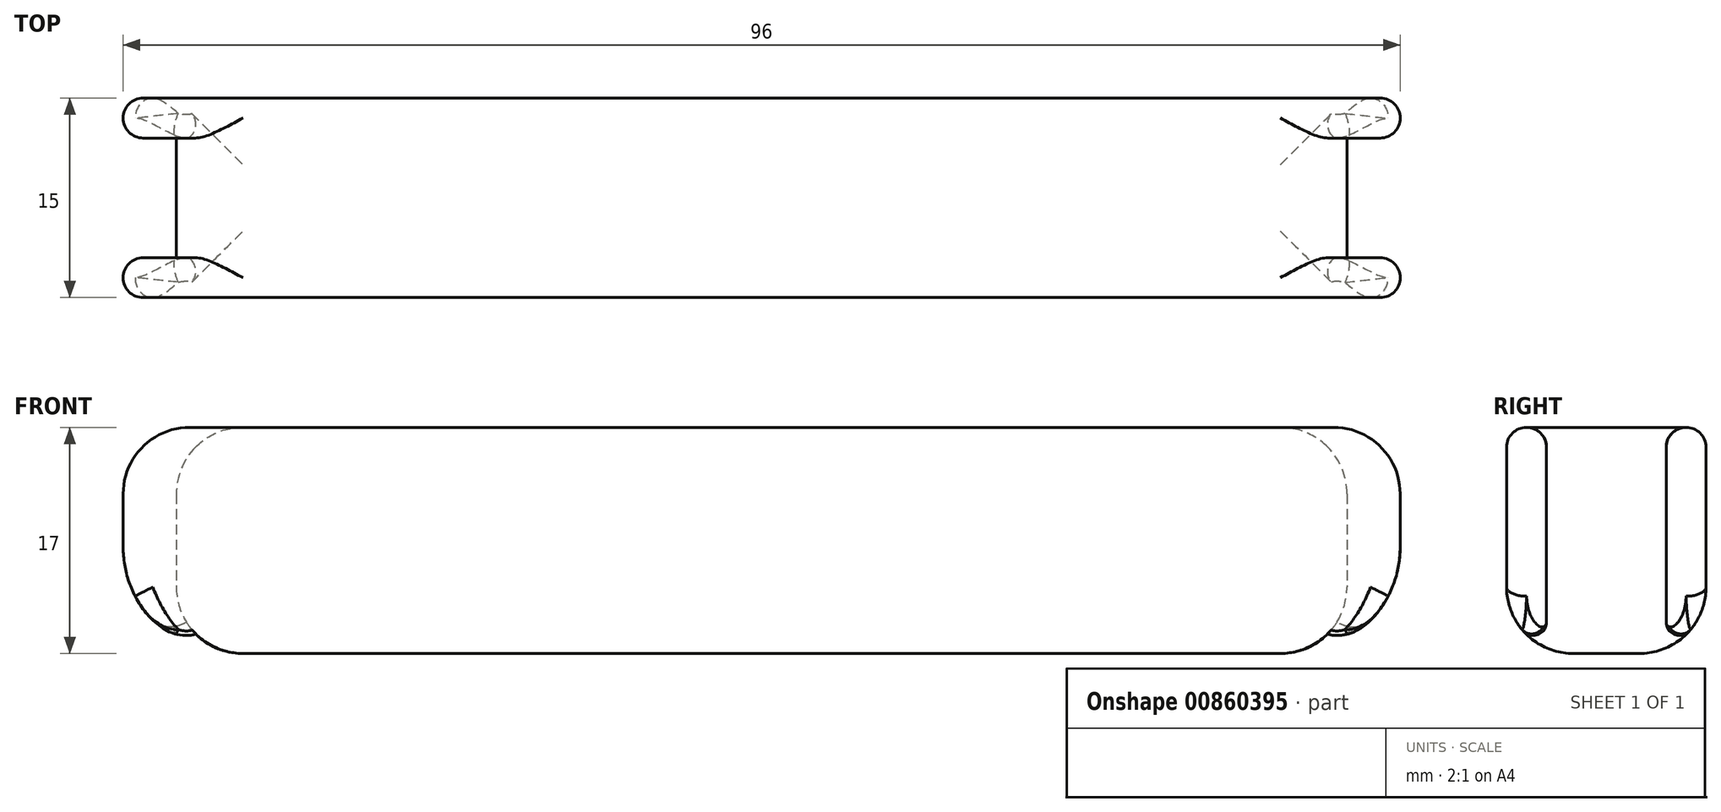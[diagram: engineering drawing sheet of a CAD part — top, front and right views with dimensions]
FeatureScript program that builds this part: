
annotation { "Feature Type Name" : "Feature", "Feature Type Description" : "" }
export const myFeature = defineFeature(function(context is Context, id is Id, definition is map)
    precondition{}
    {
        {
            var Q0;
            Q0=qCreatedBy(makeId("Top.planeOp"),FACE);
            var sketch = newSketch(context, id + "F0", { "sketchPlane" : qUnion([Q0])});
            skLineSegment(sketch, "E0.bottom", {"start": v(48, -7.5) * mm, "end": v(-48, -7.5) * mm});
            skLineSegment(sketch, "E0.top", {"start": v(48, 7.5) * mm, "end": v(-48, 7.5) * mm});
            skLineSegment(sketch, "E0.left", {"start": v(48, -7.5) * mm, "end": v(48, 7.5) * mm});
            skLineSegment(sketch, "E0.right", {"start": v(-48, -7.5) * mm, "end": v(-48, 7.5) * mm});
            skPoint(sketch, "E0.middle", {"position": v(0, 0) * mm});
            skLineSegment(sketch, "E1.bottom", {"start": v(-48, 4.5) * mm, "end": v(-44, 4.5) * mm});
            skLineSegment(sketch, "E1.top", {"start": v(-48, -4.5) * mm, "end": v(-44, -4.5) * mm});
            skLineSegment(sketch, "E1.left", {"start": v(-48, 4.5) * mm, "end": v(-48, -4.5) * mm});
            skLineSegment(sketch, "E1.right", {"start": v(-44, 4.5) * mm, "end": v(-44, -4.5) * mm});
            skLineSegment(sketch, "E2.bottom", {"start": v(48, 4.5) * mm, "end": v(44, 4.5) * mm});
            skLineSegment(sketch, "E2.top", {"start": v(48, -4.5) * mm, "end": v(44, -4.5) * mm});
            skLineSegment(sketch, "E2.left", {"start": v(48, 4.5) * mm, "end": v(48, -4.5) * mm});
            skLineSegment(sketch, "E2.right", {"start": v(44, 4.5) * mm, "end": v(44, -4.5) * mm});
            skSolve(sketch);
        }
        {
            var Q0;
            {var subQ6=sQuery(id+"F0.wireOp",EDGE,"E0.bottom");Q0=makeQuery(id+"F0.imprint","IMPRINT",FACE,{"disambiguationData":[TD([[makeQuery(id+"F0.imprint","IMPRINT",EDGE,{"derivedFrom":subQ6}),-1.0]])]});}
            extrude(context, id + "F1", {"entities" : qUnion([Q0]), "depth" : 17 * mm, "offsetDistance" : 25 * mm});
        }
        {
            var Q0;
            {var subQ0=sQuery(id+"F0.wireOp",EDGE,"E0.left");Q0=makeQuery(id+"F1.opExtrude","CAP_EDGE",EDGE,{"disambiguationData":[OSD([subQ0]),TDD([makeQuery(id+"F0.imprint","IMPRINT",EDGE,{"disambiguationData":[TD([[makeQuery(id+"F0.imprint","INTERSECT",VERTEX,{"derivedFrom":[sQuery(id+"F0.wireOp",EDGE,"E0.bottom"),subQ0]}),-1.0]])],"derivedFrom":subQ0})])],"isStart":true});}
            var Q1;
            {var subQ0=sQuery(id+"F0.wireOp",EDGE,"E0.left");Q1=makeQuery(id+"F1.opExtrude","CAP_EDGE",EDGE,{"disambiguationData":[OSD([subQ0]),TDD([makeQuery(id+"F0.imprint","IMPRINT",EDGE,{"disambiguationData":[TD([[makeQuery(id+"F0.imprint","INTERSECT",VERTEX,{"derivedFrom":[sQuery(id+"F0.wireOp",EDGE,"E0.top"),subQ0]}),1.0]])],"derivedFrom":subQ0})])],"isStart":true});}
            var Q2;
            {var subQ0=sQuery(id+"F0.wireOp",EDGE,"E0.right");Q2=makeQuery(id+"F1.opExtrude","CAP_EDGE",EDGE,{"disambiguationData":[OSD([subQ0]),TDD([makeQuery(id+"F0.imprint","IMPRINT",EDGE,{"disambiguationData":[TD([[makeQuery(id+"F0.imprint","INTERSECT",VERTEX,{"derivedFrom":[sQuery(id+"F0.wireOp",EDGE,"E0.top"),subQ0]}),1.0]])],"derivedFrom":subQ0})])],"isStart":true});}
            var Q3;
            {var subQ0=sQuery(id+"F0.wireOp",EDGE,"E0.right");Q3=makeQuery(id+"F1.opExtrude","CAP_EDGE",EDGE,{"disambiguationData":[OSD([subQ0]),TDD([makeQuery(id+"F0.imprint","IMPRINT",EDGE,{"disambiguationData":[TD([[makeQuery(id+"F0.imprint","INTERSECT",VERTEX,{"derivedFrom":[sQuery(id+"F0.wireOp",EDGE,"E0.bottom"),subQ0]}),-1.0]])],"derivedFrom":subQ0})])],"isStart":true});}
            fillet(context, id + "F2", {"entities" : qUnion([Q0, Q1, Q2, Q3]), "radius" : 8 * mm, "tangentPropagation" : true, "allowEdgeOverflow" : false});
        }
        {
            var Q0;
            {var subQ0=sQuery(id+"F0.wireOp",EDGE,"E0.right");Q0=makeQuery(id+"F2.opFillet","BLEND_EDGE",EDGE,{"blendedFrom":[makeQuery(id+"F1.opExtrude","CAP_EDGE",EDGE,{"disambiguationData":[OSD([subQ0]),TDD([makeQuery(id+"F0.imprint","IMPRINT",EDGE,{"disambiguationData":[TD([[makeQuery(id+"F0.imprint","INTERSECT",VERTEX,{"derivedFrom":[sQuery(id+"F0.wireOp",EDGE,"E0.top"),subQ0]}),1.0]])],"derivedFrom":subQ0})])],"isStart":true}),makeQuery(id+"F1.opExtrude","SWEPT_FACE",FACE,{"disambiguationData":[OSD([sQuery(id+"F0.wireOp",EDGE,"E1.right")])]})],"blendedInto":[makeQuery(id+"F1.opExtrude","SWEPT_FACE",FACE,{"disambiguationData":[OSD([sQuery(id+"F0.wireOp",EDGE,"E1.right")])]})]});}
            var Q1;
            {var subQ0=sQuery(id+"F0.wireOp",EDGE,"E0.left");Q1=makeQuery(id+"F2.opFillet","BLEND_EDGE",EDGE,{"blendedFrom":[makeQuery(id+"F1.opExtrude","CAP_EDGE",EDGE,{"disambiguationData":[OSD([subQ0]),TDD([makeQuery(id+"F0.imprint","IMPRINT",EDGE,{"disambiguationData":[TD([[makeQuery(id+"F0.imprint","INTERSECT",VERTEX,{"derivedFrom":[sQuery(id+"F0.wireOp",EDGE,"E0.bottom"),subQ0]}),-1.0]])],"derivedFrom":subQ0})])],"isStart":true}),makeQuery(id+"F1.opExtrude","SWEPT_FACE",FACE,{"disambiguationData":[OSD([sQuery(id+"F0.wireOp",EDGE,"E2.right")])]})],"blendedInto":[makeQuery(id+"F1.opExtrude","SWEPT_FACE",FACE,{"disambiguationData":[OSD([sQuery(id+"F0.wireOp",EDGE,"E2.right")])]})]});}
            var Q2;
            Q2=makeQuery(id+"F1.opExtrude","CAP_EDGE",EDGE,{"disambiguationData":[OSD([sQuery(id+"F0.wireOp",EDGE,"E1.right")])],"isStart":false});
            var Q3;
            Q3=makeQuery(id+"F1.opExtrude","CAP_EDGE",EDGE,{"disambiguationData":[OSD([sQuery(id+"F0.wireOp",EDGE,"E2.right")])],"isStart":false});
            fillet(context, id + "F3", {"entities" : qUnion([Q0, Q1, Q2, Q3]), "radius" : 5 * mm, "allowEdgeOverflow" : false});
        }
        {
            var Q0;
            Q0=makeQuery(id+"F1.opExtrude","CAP_EDGE",EDGE,{"disambiguationData":[OSD([sQuery(id+"F0.wireOp",EDGE,"E0.top")])],"isStart":true});
            var Q1;
            Q1=makeQuery(id+"F1.opExtrude","CAP_EDGE",EDGE,{"disambiguationData":[OSD([sQuery(id+"F0.wireOp",EDGE,"E0.bottom")])],"isStart":true});
            var Q2;
            {var subQ0=sQuery(id+"F0.wireOp",EDGE,"E0.right");Q2=makeQuery(id+"F1.opExtrude","CAP_EDGE",EDGE,{"disambiguationData":[OSD([subQ0]),TDD([makeQuery(id+"F0.imprint","IMPRINT",EDGE,{"disambiguationData":[TD([[makeQuery(id+"F0.imprint","INTERSECT",VERTEX,{"derivedFrom":[sQuery(id+"F0.wireOp",EDGE,"E0.top"),subQ0]}),1.0]])],"derivedFrom":subQ0})])],"isStart":false});}
            var Q3;
            {var subQ0=sQuery(id+"F0.wireOp",EDGE,"E0.right");Q3=makeQuery(id+"F1.opExtrude","CAP_EDGE",EDGE,{"disambiguationData":[OSD([subQ0]),TDD([makeQuery(id+"F0.imprint","IMPRINT",EDGE,{"disambiguationData":[TD([[makeQuery(id+"F0.imprint","INTERSECT",VERTEX,{"derivedFrom":[sQuery(id+"F0.wireOp",EDGE,"E0.bottom"),subQ0]}),-1.0]])],"derivedFrom":subQ0})])],"isStart":false});}
            var Q4;
            {var subQ0=sQuery(id+"F0.wireOp",EDGE,"E0.left");Q4=makeQuery(id+"F1.opExtrude","CAP_EDGE",EDGE,{"disambiguationData":[OSD([subQ0]),TDD([makeQuery(id+"F0.imprint","IMPRINT",EDGE,{"disambiguationData":[TD([[makeQuery(id+"F0.imprint","INTERSECT",VERTEX,{"derivedFrom":[sQuery(id+"F0.wireOp",EDGE,"E0.top"),subQ0]}),1.0]])],"derivedFrom":subQ0})])],"isStart":false});}
            var Q5;
            {var subQ0=sQuery(id+"F0.wireOp",EDGE,"E0.left");Q5=makeQuery(id+"F1.opExtrude","CAP_EDGE",EDGE,{"disambiguationData":[OSD([subQ0]),TDD([makeQuery(id+"F0.imprint","IMPRINT",EDGE,{"disambiguationData":[TD([[makeQuery(id+"F0.imprint","INTERSECT",VERTEX,{"derivedFrom":[sQuery(id+"F0.wireOp",EDGE,"E0.bottom"),subQ0]}),-1.0]])],"derivedFrom":subQ0})])],"isStart":false});}
            fillet(context, id + "F4", {"entities" : qUnion([Q0, Q1, Q2, Q3, Q4, Q5]), "radius" : 5 * mm, "allowEdgeOverflow" : false});
        }
        {
            var Q0;
            Q0=makeQuery(id+"F1.opExtrude","SWEPT_EDGE",EDGE,{"disambiguationData":[OSD([sQuery(id+"F0.wireOp",EDGE,"E0.top"),sQuery(id+"F0.wireOp",EDGE,"E0.right")])]});
            var Q1;
            Q1=makeQuery(id+"F1.opExtrude","SWEPT_EDGE",EDGE,{"disambiguationData":[OSD([sQuery(id+"F0.wireOp",EDGE,"E0.right"),sQuery(id+"F0.wireOp",EDGE,"E1.bottom"),sQuery(id+"F0.wireOp",EDGE,"E1.left")])]});
            var Q2;
            Q2=makeQuery(id+"F1.opExtrude","SWEPT_EDGE",EDGE,{"disambiguationData":[OSD([sQuery(id+"F0.wireOp",EDGE,"E0.right"),sQuery(id+"F0.wireOp",EDGE,"E1.top"),sQuery(id+"F0.wireOp",EDGE,"E1.left")])]});
            var Q3;
            {var subQ0=sQuery(id+"F0.wireOp",EDGE,"E0.bottom");var subQ1=sQuery(id+"F0.wireOp",EDGE,"E0.right");Q3=makeQuery(id+"F4.opFillet","BLEND_EDGE",EDGE,{"blendedFrom":[makeQuery(id+"F1.opExtrude","CAP_EDGE",EDGE,{"disambiguationData":[OSD([subQ1]),TDD([makeQuery(id+"F0.imprint","IMPRINT",EDGE,{"disambiguationData":[TD([[makeQuery(id+"F0.imprint","INTERSECT",VERTEX,{"derivedFrom":[subQ0,subQ1]}),-1.0]])],"derivedFrom":subQ1})])],"isStart":false}),makeQuery(id+"F1.opExtrude","SWEPT_FACE",FACE,{"disambiguationData":[OSD([subQ0])]})],"blendedInto":[makeQuery(id+"F1.opExtrude","SWEPT_FACE",FACE,{"disambiguationData":[OSD([subQ0])]})]});}
            var Q4;
            {var subQ0=sQuery(id+"F0.wireOp",EDGE,"E2.bottom");var subQ1=sQuery(id+"F0.wireOp",EDGE,"E0.left");Q4=makeQuery(id+"F4.opFillet","BLEND_EDGE",EDGE,{"blendedFrom":[makeQuery(id+"F1.opExtrude","CAP_EDGE",EDGE,{"disambiguationData":[OSD([subQ1]),TDD([makeQuery(id+"F0.imprint","IMPRINT",EDGE,{"disambiguationData":[TD([[makeQuery(id+"F0.imprint","INTERSECT",VERTEX,{"derivedFrom":[sQuery(id+"F0.wireOp",EDGE,"E0.top"),subQ1]}),1.0]])],"derivedFrom":subQ1})])],"isStart":false}),makeQuery(id+"F1.opExtrude","SWEPT_FACE",FACE,{"disambiguationData":[OSD([subQ0])]})],"blendedInto":[makeQuery(id+"F1.opExtrude","SWEPT_FACE",FACE,{"disambiguationData":[OSD([subQ0])]})]});}
            var Q5;
            {var subQ0=sQuery(id+"F0.wireOp",EDGE,"E2.top");var subQ1=sQuery(id+"F0.wireOp",EDGE,"E0.left");Q5=makeQuery(id+"F4.opFillet","BLEND_EDGE",EDGE,{"blendedFrom":[makeQuery(id+"F1.opExtrude","CAP_EDGE",EDGE,{"disambiguationData":[OSD([subQ1]),TDD([makeQuery(id+"F0.imprint","IMPRINT",EDGE,{"disambiguationData":[TD([[makeQuery(id+"F0.imprint","INTERSECT",VERTEX,{"derivedFrom":[sQuery(id+"F0.wireOp",EDGE,"E0.bottom"),subQ1]}),-1.0]])],"derivedFrom":subQ1})])],"isStart":false}),makeQuery(id+"F1.opExtrude","SWEPT_FACE",FACE,{"disambiguationData":[OSD([subQ0])]})],"blendedInto":[makeQuery(id+"F1.opExtrude","SWEPT_FACE",FACE,{"disambiguationData":[OSD([subQ0])]})]});}
            fillet(context, id + "F5", {"entities" : qUnion([Q0, Q1, Q2, Q3, Q4, Q5]), "radius" : 1.5 * mm, "tangentPropagation" : true, "allowEdgeOverflow" : false});
        }
        {
            var Q0;
            {var subQ0=sQuery(id+"F0.wireOp",EDGE,"E2.top");var subQ1=sQuery(id+"F0.wireOp",EDGE,"E0.left");var subQ2=sQuery(id+"F0.wireOp",EDGE,"E0.bottom");Q0=makeQuery(id+"F5.opFillet","BLEND_EDGE",EDGE,{"blendedFrom":[makeQuery(id+"F4.opFillet","BLEND_EDGE",EDGE,{"blendedFrom":[makeQuery(id+"F1.opExtrude","CAP_EDGE",EDGE,{"disambiguationData":[OSD([subQ2])],"isStart":true}),makeQuery(id+"F3.opFillet","SPLIT",FACE,{"disambiguationData":[OD(0.0)],"derivedFrom":makeQuery(id+"F2.opFillet","BLEND_FACE",FACE,{"disambiguationData":[OSD([subQ1])]})})],"blendedInto":[makeQuery(id+"F3.opFillet","SPLIT",FACE,{"disambiguationData":[OD(0.0)],"derivedFrom":makeQuery(id+"F2.opFillet","BLEND_FACE",FACE,{"disambiguationData":[OSD([subQ1])]})})]}),makeQuery(id+"F2.opFillet","BLEND_EDGE",EDGE,{"blendedFrom":[makeQuery(id+"F1.opExtrude","CAP_EDGE",EDGE,{"disambiguationData":[OSD([subQ1]),TDD([makeQuery(id+"F0.imprint","IMPRINT",EDGE,{"disambiguationData":[TD([[makeQuery(id+"F0.imprint","INTERSECT",VERTEX,{"derivedFrom":[subQ2,subQ1]}),-1.0]])],"derivedFrom":subQ1})])],"isStart":true}),makeQuery(id+"F1.opExtrude","SWEPT_FACE",FACE,{"disambiguationData":[OSD([subQ0])]})],"blendedInto":[makeQuery(id+"F1.opExtrude","SWEPT_FACE",FACE,{"disambiguationData":[OSD([subQ0])]})]})],"blendedInto":[]});}
            var Q1;
            {var subQ0=sQuery(id+"F0.wireOp",EDGE,"E0.left");Q1=makeQuery(id+"F5.opFillet","BLEND_EDGE",EDGE,{"blendedFrom":[makeQuery(id+"F4.opFillet","BLEND_EDGE",EDGE,{"blendedFrom":[makeQuery(id+"F1.opExtrude","CAP_EDGE",EDGE,{"disambiguationData":[OSD([sQuery(id+"F0.wireOp",EDGE,"E0.top")])],"isStart":true}),makeQuery(id+"F3.opFillet","SPLIT",FACE,{"disambiguationData":[OD(1.0)],"derivedFrom":makeQuery(id+"F2.opFillet","BLEND_FACE",FACE,{"disambiguationData":[OSD([subQ0])]})})],"blendedInto":[makeQuery(id+"F3.opFillet","SPLIT",FACE,{"disambiguationData":[OD(1.0)],"derivedFrom":makeQuery(id+"F2.opFillet","BLEND_FACE",FACE,{"disambiguationData":[OSD([subQ0])]})})]}),makeQuery(id+"F2.opFillet","BLEND_EDGE",EDGE,{"blendedFrom":[makeQuery(id+"F1.opExtrude","CAP_EDGE",EDGE,{"disambiguationData":[OSD([subQ0]),TDD([makeQuery(id+"F0.imprint","IMPRINT",EDGE,{"disambiguationData":[TD([[makeQuery(id+"F0.imprint","INTERSECT",VERTEX,{"derivedFrom":[sQuery(id+"F0.wireOp",EDGE,"E0.bottom"),subQ0]}),-1.0]])],"derivedFrom":subQ0})])],"isStart":true}),makeQuery(id+"F1.opExtrude","SWEPT_FACE",FACE,{"disambiguationData":[OSD([sQuery(id+"F0.wireOp",EDGE,"E2.bottom")])]})],"blendedInto":[makeQuery(id+"F1.opExtrude","SWEPT_FACE",FACE,{"disambiguationData":[OSD([sQuery(id+"F0.wireOp",EDGE,"E2.bottom")])]})]})],"blendedInto":[]});}
            var Q2;
            {var subQ0=sQuery(id+"F0.wireOp",EDGE,"E0.right");Q2=makeQuery(id+"F5.opFillet","BLEND_EDGE",EDGE,{"blendedFrom":[makeQuery(id+"F4.opFillet","BLEND_EDGE",EDGE,{"blendedFrom":[makeQuery(id+"F1.opExtrude","CAP_EDGE",EDGE,{"disambiguationData":[OSD([sQuery(id+"F0.wireOp",EDGE,"E0.bottom")])],"isStart":true}),makeQuery(id+"F3.opFillet","SPLIT",FACE,{"disambiguationData":[OD(0.0)],"derivedFrom":makeQuery(id+"F2.opFillet","BLEND_FACE",FACE,{"disambiguationData":[OSD([subQ0])]})})],"blendedInto":[makeQuery(id+"F3.opFillet","SPLIT",FACE,{"disambiguationData":[OD(0.0)],"derivedFrom":makeQuery(id+"F2.opFillet","BLEND_FACE",FACE,{"disambiguationData":[OSD([subQ0])]})})]}),makeQuery(id+"F2.opFillet","BLEND_EDGE",EDGE,{"blendedFrom":[makeQuery(id+"F1.opExtrude","CAP_EDGE",EDGE,{"disambiguationData":[OSD([subQ0]),TDD([makeQuery(id+"F0.imprint","IMPRINT",EDGE,{"disambiguationData":[TD([[makeQuery(id+"F0.imprint","INTERSECT",VERTEX,{"derivedFrom":[sQuery(id+"F0.wireOp",EDGE,"E0.top"),subQ0]}),1.0]])],"derivedFrom":subQ0})])],"isStart":true}),makeQuery(id+"F1.opExtrude","SWEPT_FACE",FACE,{"disambiguationData":[OSD([sQuery(id+"F0.wireOp",EDGE,"E1.top")])]})],"blendedInto":[makeQuery(id+"F1.opExtrude","SWEPT_FACE",FACE,{"disambiguationData":[OSD([sQuery(id+"F0.wireOp",EDGE,"E1.top")])]})]})],"blendedInto":[]});}
            var Q3;
            {var subQ0=sQuery(id+"F0.wireOp",EDGE,"E1.bottom");var subQ1=sQuery(id+"F0.wireOp",EDGE,"E0.right");var subQ2=sQuery(id+"F0.wireOp",EDGE,"E0.top");Q3=makeQuery(id+"F5.opFillet","BLEND_EDGE",EDGE,{"blendedFrom":[makeQuery(id+"F4.opFillet","BLEND_EDGE",EDGE,{"blendedFrom":[makeQuery(id+"F1.opExtrude","CAP_EDGE",EDGE,{"disambiguationData":[OSD([subQ2])],"isStart":true}),makeQuery(id+"F3.opFillet","SPLIT",FACE,{"disambiguationData":[OD(1.0)],"derivedFrom":makeQuery(id+"F2.opFillet","BLEND_FACE",FACE,{"disambiguationData":[OSD([subQ1])]})})],"blendedInto":[makeQuery(id+"F3.opFillet","SPLIT",FACE,{"disambiguationData":[OD(1.0)],"derivedFrom":makeQuery(id+"F2.opFillet","BLEND_FACE",FACE,{"disambiguationData":[OSD([subQ1])]})})]}),makeQuery(id+"F2.opFillet","BLEND_EDGE",EDGE,{"blendedFrom":[makeQuery(id+"F1.opExtrude","CAP_EDGE",EDGE,{"disambiguationData":[OSD([subQ1]),TDD([makeQuery(id+"F0.imprint","IMPRINT",EDGE,{"disambiguationData":[TD([[makeQuery(id+"F0.imprint","INTERSECT",VERTEX,{"derivedFrom":[subQ2,subQ1]}),1.0]])],"derivedFrom":subQ1})])],"isStart":true}),makeQuery(id+"F1.opExtrude","SWEPT_FACE",FACE,{"disambiguationData":[OSD([subQ0])]})],"blendedInto":[makeQuery(id+"F1.opExtrude","SWEPT_FACE",FACE,{"disambiguationData":[OSD([subQ0])]})]})],"blendedInto":[]});}
            fillet(context, id + "F6", {"entities" : qUnion([Q0, Q1, Q2, Q3]), "radius" : 1 * mm, "tangentPropagation" : true, "allowEdgeOverflow" : false});
        }
    });
